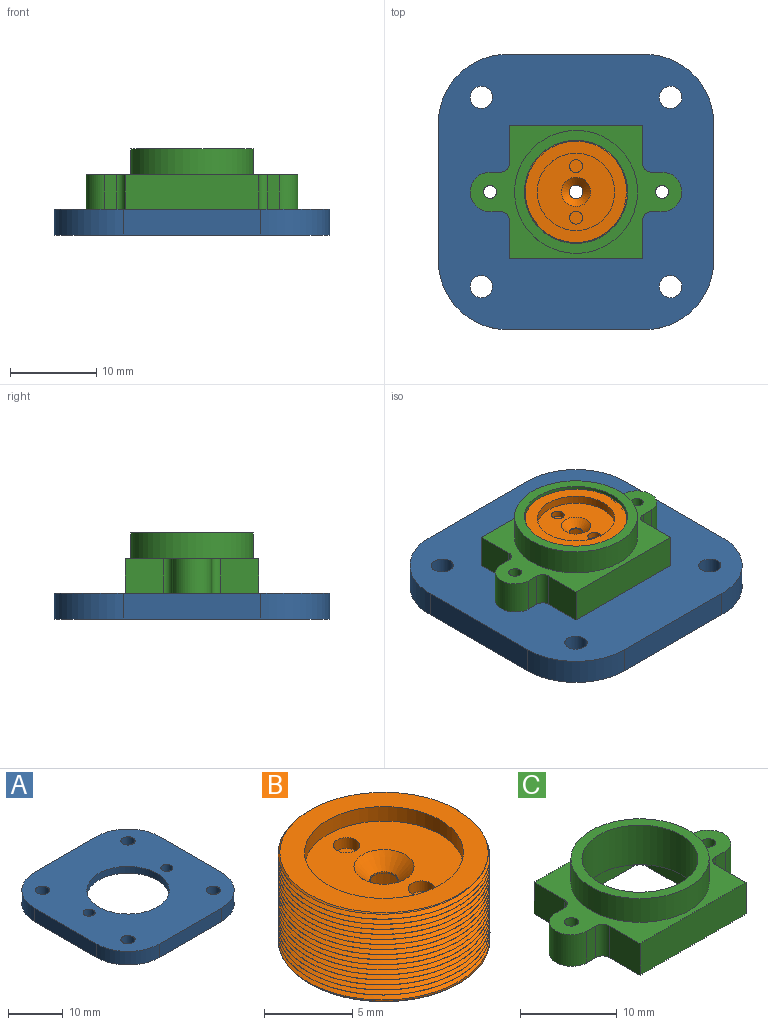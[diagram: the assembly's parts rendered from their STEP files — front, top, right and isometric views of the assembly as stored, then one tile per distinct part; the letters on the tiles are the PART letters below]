
ASSEMBLY  parts=3 mates=4
PART A: 19 faces, bbox 32x32x3 mm
  f0: cylinder r=7.5mm len=15mm, axis (0,0,1), area 70.7mm2, adj f14,f16
  f1: plane 16x3mm, normal (1,0,0), area 48mm2, adj f2,f12,f13,f14
  f2: cylinder r=8mm len=8mm, axis (0,0,1), area 37.7mm2, adj f1,f3,f13,f14
  f3: plane 16x3mm, normal (0,1,0), area 48mm2, adj f2,f4,f13,f14
  f4: cylinder r=8mm len=8mm, axis (0,0,1), area 37.7mm2, adj f3,f5,f13,f14
  f5: plane 16x3mm, normal (-1,0,0), area 48mm2, adj f4,f6,f13,f14
  f6: cylinder r=8mm len=8mm, axis (0,0,1), area 37.7mm2, adj f5,f7,f13,f14
  f7: plane 16x3mm, normal (0,-1,0), area 48mm2, adj f6,f12,f13,f14
  f8: cylinder r=1.3mm len=3mm, axis (0,0,1), area 24.5mm2, adj f13,f14
  f9: cylinder r=1.3mm len=3mm, axis (0,0,1), area 24.5mm2, adj f13,f14
  f10: cylinder r=1.3mm len=3mm, axis (0,0,1), area 24.5mm2, adj f13,f14
  f11: cylinder r=1.3mm len=3mm, axis (0,0,1), area 24.5mm2, adj f13,f14
  f12: cylinder r=8mm len=8mm, axis (0,0,1), area 37.7mm2, adj f1,f7,f13,f14
  f13: plane 32x32mm, normal (0,0,-1), area 416.9mm2, adj f1,f2,f3,f4,f5,f6,f7,f8
  f14: plane 32x32mm, normal (0,0,1), area 763.5mm2, adj f0,f1,f2,f3,f4,f5,f6,f7
  f15: cylinder r=13mm len=26mm, axis (0,0,-1), area 122.5mm2, adj f13,f16
  f16: plane 26x26mm, normal (0,0,-1), area 346.6mm2, adj f0,f15,f17,f18
  f17: cylinder r=1.1mm len=2.2mm, axis (0,0,-1), area 10.4mm2, adj f14,f16
  f18: cylinder r=1.1mm len=2.2mm, axis (0,0,-1), area 10.4mm2, adj f14,f16
PART B: 21 faces, bbox 12.1x13.9x6.4 mm
  f0: cylinder r=6mm len=12mm, axis (0,0,-1), area 9.1mm2, adj f2,f12,f17,f18,f19,f20
  f1: plane 11.87x11.87mm, normal (0,0,1), area 45.6mm2, adj f2,f4,f17,f20
  f2: cone r=5.9mm half-angle=45deg, axis (0,0,-1), area 3.6mm2, adj f0,f1,f17,f20
  f3: plane 9x9mm, normal (0,0,1), area 51mm2, adj f4,f11,f13,f15
  f4: cylinder r=4.5mm len=9mm, axis (0,0,-1), area 28.3mm2, adj f1,f3
  f5: cylinder r=5mm len=10mm, axis (0,0,1), area 31.4mm2, adj f6,f9
  f6: plane 11.8x11.8mm, normal (0,0,-1), area 30.8mm2, adj f5,f12
  f7: plane 6.5x6.5mm, normal (0,0,-1), area 31.2mm2, adj f8,f10
  f8: cylinder r=3.25mm len=6.5mm, axis (0,0,1), area 64.8mm2, adj f7,f9
  f9: plane 10x10mm, normal (0,0,-1), area 45.4mm2, adj f5,f8
  f10: cylinder r=0.8mm len=1.6mm, axis (0,0,1), area 0.5mm2, adj f7,f11
  f11: cone r=0.8mm half-angle=45deg, axis (0,0,1), area 10mm2, adj f3,f10
  f12: cone r=6mm half-angle=45deg, axis (0,0,1), area 4.2mm2, adj f0,f6,f18,f19
  f13: cylinder r=0.75mm len=1.5mm, axis (0,0,1), area 3.5mm2, adj f3,f14
  f14: plane 1.5x1.5mm, normal (0,0,1), area 1.8mm2, adj f13
  f15: cylinder r=0.75mm len=1.5mm, axis (0,0,1), area 3.5mm2, adj f3,f16
  f16: plane 1.5x1.5mm, normal (0,0,1), area 1.8mm2, adj f15
  f17: plane 0.29x0.25mm, normal (0,-1,0), area 0mm2, adj f0,f1,f2,f19,f20
  f18: plane 0.29x0.27mm, normal (0.43,0.9,0), area 0mm2, adj f0,f12,f19,f20
  f19: bspline ~13.86x12mm, area 217.2mm2, adj f0,f12,f17,f18,f20
  f20: bspline ~13.86x12mm, area 212.1mm2, adj f0,f1,f2,f17,f18,f19
PART C: 32 faces, bbox 24.6x15.5x7 mm
  f0: plane 24.6x15.5mm, normal (0,0,-1), area 105.4mm2, adj f2,f3,f4,f5,f6,f7,f8,f9
  f1: cylinder r=6mm len=12mm, axis (0,0,1), area 188.5mm2, adj f22,f31
  f2: cylinder r=1mm len=4mm, axis (0,0,-1), area 6.3mm2, adj f0,f3,f18,f20
  f3: plane 4.45x4mm, normal (-1,0,0), area 17.8mm2, adj f0,f2,f4,f20
  f4: plane 15.5x4mm, normal (0,-1,0), area 62mm2, adj f0,f3,f5,f20
  f5: plane 4.45x4mm, normal (1,0,0), area 17.8mm2, adj f0,f4,f6,f20
  f6: cylinder r=1mm len=4mm, axis (0,0,-1), area 6.3mm2, adj f0,f5,f7,f20
  f7: plane 4x1.39mm, normal (0,-1,0), area 5.6mm2, adj f0,f6,f8,f20
  f8: cylinder r=2.3mm len=4.6mm, axis (0,0,-1), area 28.5mm2, adj f0,f7,f9,f20
  f9: plane 4x1.21mm, normal (0,1,0), area 4.8mm2, adj f0,f8,f10,f20
  f10: cylinder r=1mm len=4mm, axis (0,0,-1), area 6.3mm2, adj f0,f9,f11,f20
  f11: plane 4.45x4mm, normal (1,0,0), area 17.8mm2, adj f0,f10,f12,f20
  f12: plane 15.5x4mm, normal (0,1,0), area 62mm2, adj f0,f11,f13,f20
  f13: plane 4.45x4mm, normal (-1,0,0), area 17.8mm2, adj f0,f12,f14,f20
  f14: cylinder r=1mm len=4mm, axis (0,0,-1), area 6.3mm2, adj f0,f13,f15,f20
  f15: plane 4x1.21mm, normal (0,1,0), area 4.8mm2, adj f0,f14,f16,f20
  f16: cylinder r=2.3mm len=4.6mm, axis (0,0,-1), area 28.5mm2, adj f0,f15,f18,f20
  f17: cylinder r=0.75mm len=4mm, axis (0,0,-1), area 18.8mm2, adj f0,f20
  f18: plane 4x1.39mm, normal (0,-1,0), area 5.6mm2, adj f0,f2,f16,f20
  f19: cylinder r=0.75mm len=4mm, axis (0,0,-1), area 18.8mm2, adj f0,f20
  f20: plane 24.6x15.5mm, normal (0,0,1), area 114.3mm2, adj f2,f3,f4,f5,f6,f7,f8,f9
  f21: cylinder r=7.15mm len=14.3mm, axis (0,0,-1), area 134.8mm2, adj f20,f22
  f22: plane 14.3x14.3mm, normal (0,0,1), area 47.5mm2, adj f1,f21
  f23: plane 11.05x2mm, normal (-1,0,0), area 22.1mm2, adj f0,f24,f30,f31
  f24: cylinder r=1mm len=2mm, axis (0,0,-1), area 3.1mm2, adj f0,f23,f25,f31
  f25: plane 11.05x2mm, normal (0,1,0), area 22.1mm2, adj f0,f24,f26,f31
  f26: cylinder r=1mm len=2mm, axis (0,0,-1), area 3.1mm2, adj f0,f25,f27,f31
  f27: plane 11.05x2mm, normal (1,0,0), area 22.1mm2, adj f0,f26,f28,f31
  f28: cylinder r=1mm len=2mm, axis (0,0,-1), area 3.1mm2, adj f0,f27,f29,f31
  f29: plane 11.05x2mm, normal (0,-1,0), area 22.1mm2, adj f0,f28,f30,f31
  f30: cylinder r=1mm len=2mm, axis (0,0,-1), area 3.1mm2, adj f0,f23,f29,f31
  f31: plane 13.05x13.05mm, normal (0,0,-1), area 56.3mm2, adj f1,f23,f24,f25,f26,f27,f28,f29
PLACE A t=(6.91,9.21,1.6)mm
PLACE B t=(6.91,9.21,6.27)mm
PLACE C t=(6.91,9.21,1.6)mm
MATE cylindrical C.f1 <-> A.f0  axis (0,0,1) through (6.91,9.21,8.6)mm
MATE planar B.f0 <-> A.f15  axis (0,0,-1) through (6.91,9.21,2.1)mm
MATE planar C.f1 <-> A.f0  axis (0,0,-1) through (6.91,9.21,1.6)mm
MATE cylindrical B.f4 <-> C.f1  axis (0,0,1) through (6.91,9.21,7.27)mm
